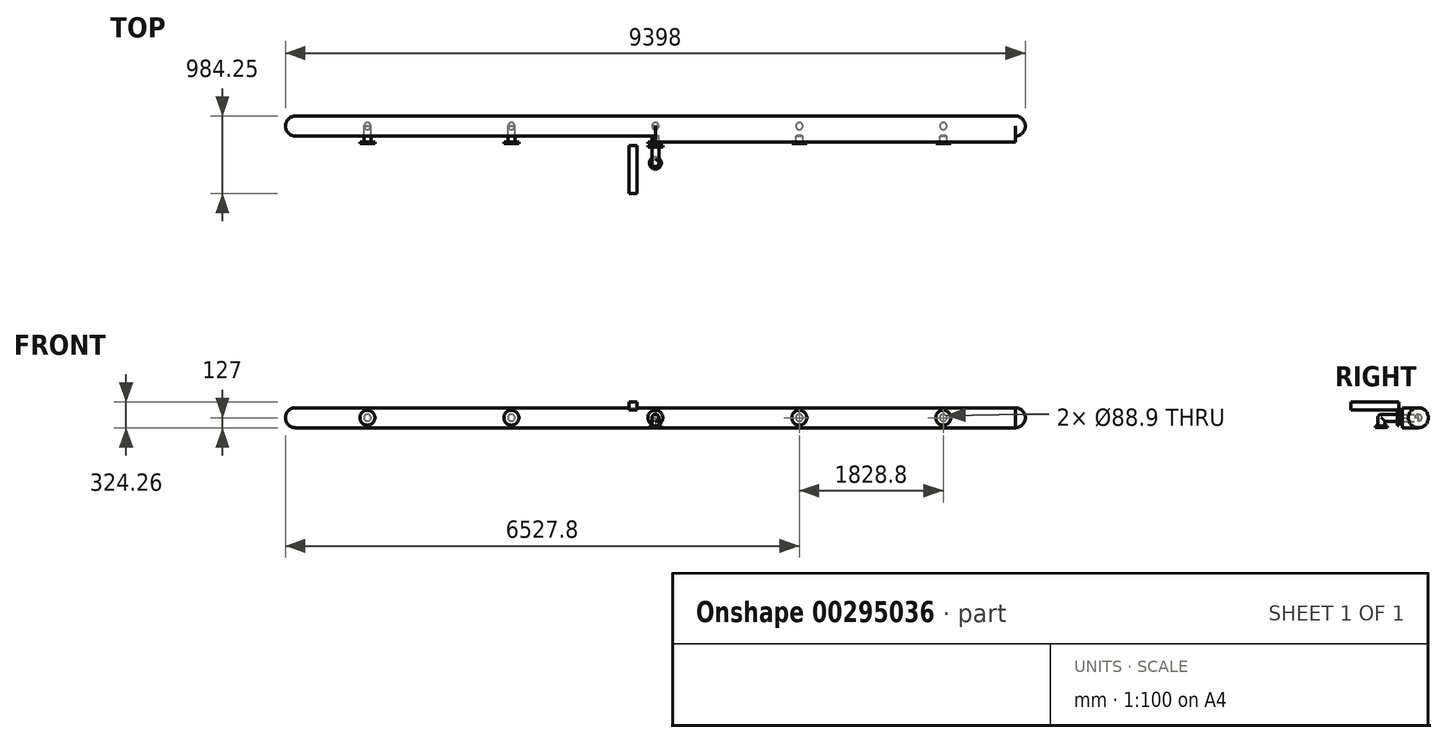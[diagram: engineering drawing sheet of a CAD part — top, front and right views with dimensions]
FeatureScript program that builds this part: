
annotation { "Feature Type Name" : "Feature", "Feature Type Description" : "" }
export const myFeature = defineFeature(function(context is Context, id is Id, definition is map)
    precondition{}
    {
        {
            var Q0;
            Q0=qCreatedBy(makeId("Front.planeOp"),FACE);
            var sketch = newSketch(context, id + "F0", { "sketchPlane" : qUnion([Q0])});
            skLineSegment(sketch, "E0.bottom", {"start": v(-4572, -127) * mm, "end": v(4572, -127) * mm});
            skLineSegment(sketch, "E0.top", {"start": v(-4572, 127) * mm, "end": v(4572, 127) * mm});
            skLineSegment(sketch, "E0.left", {"start": v(-4572, -127) * mm, "end": v(-4572, 127) * mm});
            skLineSegment(sketch, "E0.right", {"start": v(4572, -127) * mm, "end": v(4572, 127) * mm});
            skPoint(sketch, "E0.middle", {"position": v(0, 0) * mm});
            skCircle(sketch, "E1", {"center": v(0, 0) * mm, "radius": 44.45 * mm});
            skLineSegment(sketch, "E2", {"start": v(0, 0) * mm, "end": v(-1828.8, 0) * mm});
            skCircle(sketch, "E3", {"center": v(-1828.8, 0) * mm, "radius": 44.45 * mm});
            skLineSegment(sketch, "E4", {"start": v(-1828.8, 0) * mm, "end": v(-3657.6, 0) * mm});
            skCircle(sketch, "E5", {"center": v(-3657.6, 0) * mm, "radius": 44.45 * mm});
            skLineSegment(sketch, "E6", {"start": v(0, 127) * mm, "end": v(0, -127) * mm});
            skCircle(sketch, "E7.MirrorC", {"center": v(1828.8, 0) * mm, "radius": 44.45 * mm});
            skCircle(sketch, "E8.MirrorC", {"center": v(3657.6, 0) * mm, "radius": 44.45 * mm});
            skLineSegment(sketch, "E9", {"start": v(-3657.6, 0) * mm, "end": v(-4572, 0) * mm});
            skLineSegment(sketch, "E10", {"start": v(0, 0) * mm, "end": v(4572, 0) * mm});
            skSolve(sketch);
        }
        {
            var Q0;
            {var subQ5=sQuery(id+"F0.wireOp",EDGE,"E0.left");var subQ6=sQuery(id+"F0.wireOp",EDGE,"E0.top");var subQ7=makeQuery(id+"F0.imprint","INTERSECT",VERTEX,{"derivedFrom":[subQ6,subQ5]});Q0=makeQuery(id+"F0.imprint","IMPRINT",FACE,{"disambiguationData":[TD([[makeQuery(id+"F0.imprint","IMPRINT",EDGE,{"disambiguationData":[TD([[subQ7,-1.0]])],"derivedFrom":subQ6}),-1.0]])]});}
            var Q1;
            {var subQ1=sQuery(id+"F0.wireOp",EDGE,"E0.top");var subQ9=sQuery(id+"F0.wireOp",EDGE,"E0.right");var subQ10=makeQuery(id+"F0.imprint","INTERSECT",VERTEX,{"derivedFrom":[subQ1,subQ9]});Q1=makeQuery(id+"F0.imprint","IMPRINT",FACE,{"disambiguationData":[TD([[makeQuery(id+"F0.imprint","IMPRINT",EDGE,{"disambiguationData":[TD([[subQ10,1.0]])],"derivedFrom":subQ1}),-1.0]])]});}
            var Q2;
            Q2=sQuery(id+"F0.wireOp",EDGE,"E2");
            revolve(context, id + "F1", {"entities" : qUnion([Q0, Q1]), "axis" : qUnion([Q2]), "revolveType" : RevolveType.FULL});
        }
        {
            var Q0;
            {var subQ0=sQuery(id+"F0.wireOp",EDGE,"E9");var subQ1=sQuery(id+"F0.wireOp",EDGE,"E4");var subQ2=makeQuery(id+"F0.imprint","INTERSECT",VERTEX,{"derivedFrom":[subQ1,subQ0]});Q0=makeQuery(id+"F0.imprint","IMPRINT",FACE,{"disambiguationData":[TD([[makeQuery(id+"F0.imprint","IMPRINT",EDGE,{"disambiguationData":[TD([[subQ2,1.0]])],"derivedFrom":subQ1}),-1.0]])]});}
            var Q1;
            {var subQ0=sQuery(id+"F0.wireOp",EDGE,"E9");var subQ1=sQuery(id+"F0.wireOp",EDGE,"E4");var subQ2=makeQuery(id+"F0.imprint","INTERSECT",VERTEX,{"derivedFrom":[subQ1,subQ0]});Q1=makeQuery(id+"F0.imprint","IMPRINT",FACE,{"disambiguationData":[TD([[makeQuery(id+"F0.imprint","IMPRINT",EDGE,{"disambiguationData":[TD([[subQ2,1.0]])],"derivedFrom":subQ1}),1.0]])]});}
            var Q2;
            {var subQ0=sQuery(id+"F0.wireOp",EDGE,"E4");var subQ1=sQuery(id+"F0.wireOp",EDGE,"E2");var subQ2=makeQuery(id+"F0.imprint","INTERSECT",VERTEX,{"derivedFrom":[subQ1,subQ0]});Q2=makeQuery(id+"F0.imprint","IMPRINT",FACE,{"disambiguationData":[TD([[makeQuery(id+"F0.imprint","IMPRINT",EDGE,{"disambiguationData":[TD([[subQ2,1.0]])],"derivedFrom":subQ1}),-1.0]])]});}
            var Q3;
            {var subQ0=sQuery(id+"F0.wireOp",EDGE,"E4");var subQ1=sQuery(id+"F0.wireOp",EDGE,"E2");var subQ2=makeQuery(id+"F0.imprint","INTERSECT",VERTEX,{"derivedFrom":[subQ1,subQ0]});Q3=makeQuery(id+"F0.imprint","IMPRINT",FACE,{"disambiguationData":[TD([[makeQuery(id+"F0.imprint","IMPRINT",EDGE,{"disambiguationData":[TD([[subQ2,1.0]])],"derivedFrom":subQ1}),1.0]])]});}
            var Q4;
            {var subQ0=sQuery(id+"F0.wireOp",EDGE,"E6");var subQ1=sQuery(id+"F0.wireOp",EDGE,"E1");var subQ2=makeQuery(id+"F0.imprint","INTERSECT",VERTEX,{"disambiguationData":[OD(0.0)],"derivedFrom":[subQ1,subQ0]});Q4=makeQuery(id+"F0.imprint","IMPRINT",FACE,{"disambiguationData":[TD([[makeQuery(id+"F0.imprint","IMPRINT",EDGE,{"disambiguationData":[TD([[subQ2,1.0]])],"derivedFrom":subQ1}),1.0]])]});}
            var Q5;
            {var subQ0=sQuery(id+"F0.wireOp",EDGE,"E6");var subQ1=sQuery(id+"F0.wireOp",EDGE,"E1");var subQ2=makeQuery(id+"F0.imprint","INTERSECT",VERTEX,{"disambiguationData":[OD(0.0)],"derivedFrom":[subQ1,subQ0]});Q5=makeQuery(id+"F0.imprint","IMPRINT",FACE,{"disambiguationData":[TD([[makeQuery(id+"F0.imprint","IMPRINT",EDGE,{"disambiguationData":[TD([[subQ2,-1.0]])],"derivedFrom":subQ1}),1.0]])]});}
            var Q6;
            {var subQ0=sQuery(id+"F0.wireOp",EDGE,"E2");var subQ1=sQuery(id+"F0.wireOp",EDGE,"E1");var subQ2=makeQuery(id+"F0.imprint","INTERSECT",VERTEX,{"derivedFrom":[subQ1,subQ0]});Q6=makeQuery(id+"F0.imprint","IMPRINT",FACE,{"disambiguationData":[TD([[makeQuery(id+"F0.imprint","IMPRINT",EDGE,{"disambiguationData":[TD([[subQ2,-1.0]])],"derivedFrom":subQ1}),1.0]])]});}
            var Q7;
            {var subQ0=sQuery(id+"F0.wireOp",EDGE,"E10");var subQ1=sQuery(id+"F0.wireOp",EDGE,"E1");var subQ2=makeQuery(id+"F0.imprint","INTERSECT",VERTEX,{"derivedFrom":[subQ1,subQ0]});Q7=makeQuery(id+"F0.imprint","IMPRINT",FACE,{"disambiguationData":[TD([[makeQuery(id+"F0.imprint","IMPRINT",EDGE,{"disambiguationData":[TD([[subQ2,1.0]])],"derivedFrom":subQ1}),1.0]])]});}
            var Q8;
            {var subQ0=sQuery(id+"F0.wireOp",EDGE,"E10");var subQ1=sQuery(id+"F0.wireOp",EDGE,"E7.MirrorC");var subQ2=makeQuery(id+"F0.imprint","INTERSECT",VERTEX,{"disambiguationData":[OD(0.0)],"derivedFrom":[subQ1,subQ0]});Q8=makeQuery(id+"F0.imprint","IMPRINT",FACE,{"disambiguationData":[TD([[makeQuery(id+"F0.imprint","IMPRINT",EDGE,{"disambiguationData":[TD([[subQ2,-1.0]])],"derivedFrom":subQ1}),-1.0]])]});}
            var Q9;
            {var subQ0=sQuery(id+"F0.wireOp",EDGE,"E10");var subQ1=sQuery(id+"F0.wireOp",EDGE,"E7.MirrorC");var subQ2=makeQuery(id+"F0.imprint","INTERSECT",VERTEX,{"disambiguationData":[OD(0.0)],"derivedFrom":[subQ1,subQ0]});Q9=makeQuery(id+"F0.imprint","IMPRINT",FACE,{"disambiguationData":[TD([[makeQuery(id+"F0.imprint","IMPRINT",EDGE,{"disambiguationData":[TD([[subQ2,1.0]])],"derivedFrom":subQ1}),-1.0]])]});}
            var Q10;
            {var subQ0=sQuery(id+"F0.wireOp",EDGE,"E10");var subQ1=sQuery(id+"F0.wireOp",EDGE,"E8.MirrorC");var subQ2=makeQuery(id+"F0.imprint","INTERSECT",VERTEX,{"disambiguationData":[OD(0.0)],"derivedFrom":[subQ1,subQ0]});Q10=makeQuery(id+"F0.imprint","IMPRINT",FACE,{"disambiguationData":[TD([[makeQuery(id+"F0.imprint","IMPRINT",EDGE,{"disambiguationData":[TD([[subQ2,-1.0]])],"derivedFrom":subQ1}),-1.0]])]});}
            var Q11;
            {var subQ0=sQuery(id+"F0.wireOp",EDGE,"E10");var subQ1=sQuery(id+"F0.wireOp",EDGE,"E8.MirrorC");var subQ2=makeQuery(id+"F0.imprint","INTERSECT",VERTEX,{"disambiguationData":[OD(0.0)],"derivedFrom":[subQ1,subQ0]});Q11=makeQuery(id+"F0.imprint","IMPRINT",FACE,{"disambiguationData":[TD([[makeQuery(id+"F0.imprint","IMPRINT",EDGE,{"disambiguationData":[TD([[subQ2,1.0]])],"derivedFrom":subQ1}),-1.0]])]});}
            extrude(context, id + "F2", {"entities" : qUnion([Q0, Q1, Q2, Q3, Q4, Q5, Q6, Q7, Q8, Q9, Q10, Q11]), "depth" : 203.2 * mm});
        }
        {
            var Q0;
            Q0=makeQuery(id+"F2.opExtrude","CAP_FACE",FACE,{"disambiguationData":[OSD([sQuery(id+"F0.wireOp",EDGE,"E5")])],"isStart":false});
            var sketch = newSketch(context, id + "F3", { "sketchPlane" : qUnion([Q0])});
            skCircle(sketch, "E11", {"center": v(-3657.6, 0) * mm, "radius": 95.25 * mm});
            skLineSegment(sketch, "E12", {"start": v(-3657.6, 0) * mm, "end": v(-1828.8, 0) * mm});
            skLineSegment(sketch, "E13", {"start": v(-1828.8, 0) * mm, "end": v(0, 0) * mm});
            skLineSegment(sketch, "E14", {"start": v(0, 0) * mm, "end": v(1828.8, 0) * mm});
            skLineSegment(sketch, "E15", {"start": v(1828.8, 0) * mm, "end": v(3657.6, 0) * mm});
            skCircle(sketch, "E16", {"center": v(-1828.8, 0) * mm, "radius": 95.25 * mm});
            skCircle(sketch, "E17", {"center": v(0, 0) * mm, "radius": 95.25 * mm});
            skCircle(sketch, "E18", {"center": v(1828.8, 0) * mm, "radius": 95.25 * mm});
            skCircle(sketch, "E19", {"center": v(3657.6, 0) * mm, "radius": 95.25 * mm});
            skSolve(sketch);
        }
        {
            var Q0;
            Q0 = qSketchRegion(id + "F3", true);
            extrude(context, id + "F4", {"entities" : qUnion([Q0]), "depth" : 19.05 * mm});
        }
        {
            var Q0;
            Q0=makeQuery(id+"F1.opRevolve","SWEPT_FACE",FACE,{"disambiguationData":[OSD([sQuery(id+"F0.wireOp",EDGE,"E0.left")])]});
            var sketch = newSketch(context, id + "F5", { "sketchPlane" : qUnion([Q0])});
            skLineSegment(sketch, "E20", {"start": v(0, 127) * mm, "end": v(0, -127) * mm});
            skSolve(sketch);
        }
        {
            var Q0;
            {var subQ0=sQuery(id+"F5.wireOp",EDGE,"E20");Q0=makeQuery(id+"F5.imprint","IMPRINT",FACE,{"disambiguationData":[TD([[makeQuery(id+"F5.imprint","IMPRINT",EDGE,{"derivedFrom":subQ0}),-1.0]])]});}
            var Q1;
            Q1=sQuery(id+"F5.wireOp",EDGE,"E20");
            revolve(context, id + "F6", {"operationType" : NewBodyOperationType.ADD, "entities" : qUnion([Q0]), "axis" : qUnion([Q1]), "revolveType" : RevolveType.FULL});
        }
        {
            var Q0;
            Q0=makeQuery(id+"F1.opRevolve","SWEPT_FACE",FACE,{"disambiguationData":[OSD([sQuery(id+"F0.wireOp",EDGE,"E0.right")])]});
            var sketch = newSketch(context, id + "F7", { "sketchPlane" : qUnion([Q0])});
            skLineSegment(sketch, "E21", {"start": v(0, 127) * mm, "end": v(0, -127) * mm});
            skSolve(sketch);
        }
        {
            var Q0;
            {var subQ0=sQuery(id+"F7.wireOp",EDGE,"E21");Q0=makeQuery(id+"F7.imprint","IMPRINT",FACE,{"disambiguationData":[TD([[makeQuery(id+"F7.imprint","IMPRINT",EDGE,{"derivedFrom":subQ0}),-1.0]])]});}
            var Q1;
            Q1=sQuery(id+"F7.wireOp",EDGE,"E21");
            revolve(context, id + "F8", {"operationType" : NewBodyOperationType.ADD, "entities" : qUnion([Q0]), "axis" : qUnion([Q1]), "revolveType" : RevolveType.FULL});
        }
        {
            var Q0;
            Q0=makeQuery(id+"F4.opExtrude","CAP_FACE",FACE,{"disambiguationData":[OSD([sQuery(id+"F3.wireOp",EDGE,"E17")])],"isStart":false});
            cPlane(context, id + "F9", {"entities" : qUnion([Q0]), "cplaneType" : CPlaneType.OFFSET, "offset" : 25.4 * mm, "width" : 152.4 * mm, "height" : 152.4 * mm});
        }
        {
            var Q0;
            Q0=qCreatedBy(id+"F9.planeOp",FACE);
            var sketch = newSketch(context, id + "F10", { "sketchPlane" : qUnion([Q0])});
            skCircle(sketch, "E22", {"center": v(0, 0) * mm, "radius": 95.25 * mm});
            skSolve(sketch);
        }
        {
            var Q0;
            Q0 = qSketchRegion(id + "F10", true);
            extrude(context, id + "F11", {"entities" : qUnion([Q0]), "depth" : 19.05 * mm});
        }
        {
            var Q0;
            Q0=makeQuery(id+"F11.opExtrude","CAP_FACE",FACE,{"disambiguationData":[OSD([sQuery(id+"F10.wireOp",EDGE,"E22")])],"isStart":false});
            var sketch = newSketch(context, id + "F12", { "sketchPlane" : qUnion([Q0])});
            skCircle(sketch, "E23", {"center": v(0, 0) * mm, "radius": 44.45 * mm});
            skSolve(sketch);
        }
        {
            var Q0;
            Q0 = qSketchRegion(id + "F12", true);
            extrude(context, id + "F13", {"entities" : qUnion([Q0]), "operationType" : NewBodyOperationType.ADD, "depth" : 203.2 * mm});
        }
        {
            var Q0;
            Q0=makeQuery(id+"F13.opExtrude","CAP_FACE",FACE,{"disambiguationData":[OSD([sQuery(id+"F12.wireOp",EDGE,"E23")])],"isStart":false});
            var sketch = newSketch(context, id + "F14", { "sketchPlane" : qUnion([Q0])});
            skLineSegment(sketch, "E24", {"start": v(-44.45, 0) * mm, "end": v(44.45, 0) * mm});
            skSolve(sketch);
        }
        {
            var Q0;
            {var subQ0=sQuery(id+"F14.wireOp",EDGE,"E24");Q0=makeQuery(id+"F14.imprint","IMPRINT",FACE,{"disambiguationData":[TD([[makeQuery(id+"F14.imprint","IMPRINT",EDGE,{"derivedFrom":subQ0}),1.0]])]});}
            var Q1;
            Q1=sQuery(id+"F14.wireOp",EDGE,"E24");
            revolve(context, id + "F15", {"operationType" : NewBodyOperationType.ADD, "entities" : qUnion([Q0]), "axis" : qUnion([Q1]), "revolveType" : RevolveType.ONE_DIRECTION, "angle" : 90 * degree});
        }
        {
            var Q0;
            Q0=makeQuery(id+"F15.opRevolve","CAP_FACE",FACE,{"disambiguationData":[OSD([sQuery(id+"F12.wireOp",EDGE,"E23"),sQuery(id+"F14.wireOp",EDGE,"E24")])],"isStart":false});
            var sketch = newSketch(context, id + "F16", { "sketchPlane" : qUnion([Q0])});
            skCircle(sketch, "E25", {"center": v(0, 469.9) * mm, "radius": 44.45 * mm});
            skSolve(sketch);
        }
        {
            var Q0;
            Q0 = qSketchRegion(id + "F16", true);
            extrude(context, id + "F17", {"entities" : qUnion([Q0]), "operationType" : NewBodyOperationType.ADD, "depth" : 101.6 * mm});
        }
        {
            var Q0;
            Q0=makeQuery(id+"F17.opExtrude","CAP_FACE",FACE,{"disambiguationData":[OSD([sQuery(id+"F16.wireOp",EDGE,"E25")])],"isStart":false});
            var sketch = newSketch(context, id + "F18", { "sketchPlane" : qUnion([Q0])});
            skCircle(sketch, "E26", {"center": v(0, 469.9) * mm, "radius": 76.2 * mm});
            skSolve(sketch);
        }
        {
            var Q0;
            Q0 = qSketchRegion(id + "F18", true);
            extrude(context, id + "F19", {"entities" : qUnion([Q0]), "operationType" : NewBodyOperationType.ADD, "depth" : 19.05 * mm});
        }
        {
            var Q0;
            Q0=qCreatedBy(id+"F9.planeOp",FACE);
            var sketch = newSketch(context, id + "F20", { "sketchPlane" : qUnion([Q0])});
            skLineSegment(sketch, "E27.bottom", {"start": v(-230.79, 95.66) * mm, "end": v(-332.39, 95.66) * mm});
            skLineSegment(sketch, "E27.top", {"start": v(-230.79, 197.26) * mm, "end": v(-332.39, 197.26) * mm});
            skLineSegment(sketch, "E27.left", {"start": v(-230.79, 95.66) * mm, "end": v(-230.79, 197.26) * mm});
            skLineSegment(sketch, "E27.right", {"start": v(-332.39, 95.66) * mm, "end": v(-332.39, 197.26) * mm});
            skPoint(sketch, "E27.middle", {"position": v(-281.59, 146.46) * mm});
            skSolve(sketch);
        }
        {
            var Q0;
            Q0 = qSketchRegion(id + "F20", true);
            extrude(context, id + "F21", {"entities" : qUnion([Q0]), "depth" : 609.6 * mm});
        }
    });
